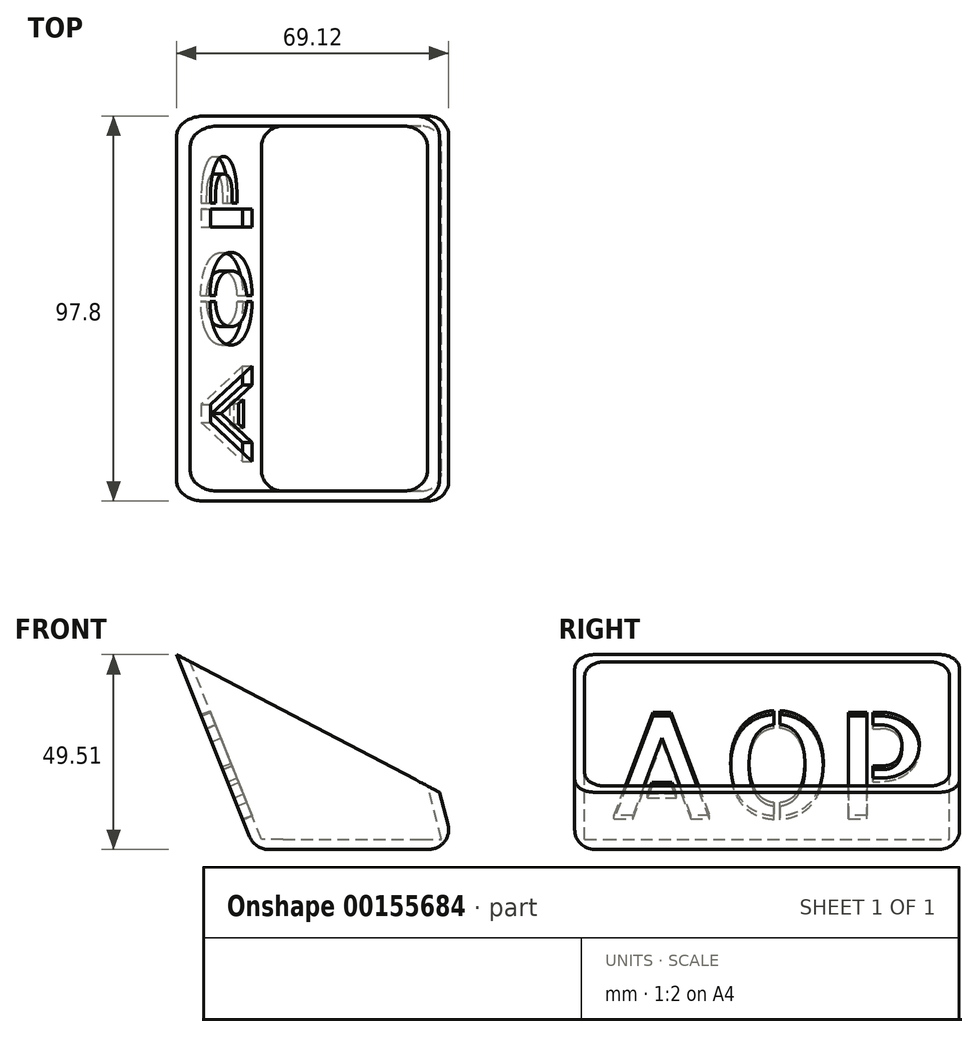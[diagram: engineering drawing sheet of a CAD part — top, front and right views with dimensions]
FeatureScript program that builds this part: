
annotation { "Feature Type Name" : "Feature", "Feature Type Description" : "" }
export const myFeature = defineFeature(function(context is Context, id is Id, definition is map)
    precondition{}
    {
        {
            var Q0;
            Q0=qCreatedBy(makeId("Front.planeOp"),FACE);
            var sketch = newSketch(context, id + "F0", { "sketchPlane" : qUnion([Q0])});
            skLineSegment(sketch, "E0", {"start": v(-16.22, 0) * mm, "end": v(34.58, 0) * mm});
            skLineSegment(sketch, "E1", {"start": v(34.58, 0) * mm, "end": v(30.69, 14.52) * mm});
            skLineSegment(sketch, "E2", {"start": v(-16.22, 0) * mm, "end": v(-36.08, 49.5) * mm});
            skLineSegment(sketch, "E3", {"start": v(-36.08, 49.5) * mm, "end": v(30.69, 14.52) * mm});
            skSolve(sketch);
        }
        {
            var Q0;
            Q0 = qSketchRegion(id + "F0", true);
            extrude(context, id + "F1", {"entities" : qUnion([Q0]), "endBound" : BoundingType.SYMMETRIC, "depth" : 97.8 * mm});
        }
        {
            var Q0;
            Q0=makeQuery(id+"F1.opExtrude","SWEPT_FACE",FACE,{"disambiguationData":[OSD([sQuery(id+"F0.wireOp",EDGE,"E3")])]});
            shell(context, id + "F2", {"entities" : qUnion([Q0]), "thickness" : 2.54 * mm});
        }
        {
            var Q0;
            Q0=makeQuery(id+"F1.opExtrude","CAP_EDGE",EDGE,{"disambiguationData":[OSD([sQuery(id+"F0.wireOp",EDGE,"E2")])],"isStart":false});
            var Q1;
            Q1=makeQuery(id+"F1.opExtrude","CAP_EDGE",EDGE,{"disambiguationData":[OSD([sQuery(id+"F0.wireOp",EDGE,"E1")])],"isStart":false});
            var Q2;
            Q2=makeQuery(id+"F1.opExtrude","CAP_EDGE",EDGE,{"disambiguationData":[OSD([sQuery(id+"F0.wireOp",EDGE,"E1")])],"isStart":true});
            var Q3;
            Q3=makeQuery(id+"F1.opExtrude","CAP_EDGE",EDGE,{"disambiguationData":[OSD([sQuery(id+"F0.wireOp",EDGE,"E2")])],"isStart":true});
            var Q4;
            Q4=makeQuery(id+"F1.opExtrude","SWEPT_EDGE",EDGE,{"disambiguationData":[OSD([sQuery(id+"F0.wireOp",EDGE,"E0"),sQuery(id+"F0.wireOp",EDGE,"E2")])]});
            var Q5;
            Q5=makeQuery(id+"F1.opExtrude","CAP_EDGE",EDGE,{"disambiguationData":[OSD([sQuery(id+"F0.wireOp",EDGE,"E0")])],"isStart":false});
            var Q6;
            Q6=makeQuery(id+"F1.opExtrude","CAP_EDGE",EDGE,{"disambiguationData":[OSD([sQuery(id+"F0.wireOp",EDGE,"E0")])],"isStart":true});
            var Q7;
            Q7=makeQuery(id+"F1.opExtrude","SWEPT_EDGE",EDGE,{"disambiguationData":[OSD([sQuery(id+"F0.wireOp",EDGE,"E0"),sQuery(id+"F0.wireOp",EDGE,"E1")])]});
            fillet(context, id + "F3", {"entities" : qUnion([Q0, Q1, Q2, Q3, Q4, Q5, Q6, Q7]), "radius" : 5.08 * mm, "tangentPropagation" : true, "allowEdgeOverflow" : false});
        }
        {
            var Q0;
            {var subQ0=sQuery(id+"F0.wireOp",EDGE,"E2");Q0=makeQuery(id+"F2.opShell","OFFSET_EDGE",EDGE,{"disambiguationData":[OSD([subQ0]),TDD([makeQuery(id+"F1.opExtrude","CAP_EDGE",EDGE,{"disambiguationData":[OSD([subQ0])],"isStart":false})])]});}
            var Q1;
            {var subQ0=sQuery(id+"F0.wireOp",EDGE,"E2");Q1=makeQuery(id+"F2.opShell","OFFSET_EDGE",EDGE,{"disambiguationData":[OSD([subQ0]),TDD([makeQuery(id+"F1.opExtrude","CAP_EDGE",EDGE,{"disambiguationData":[OSD([subQ0])],"isStart":true})])]});}
            var Q2;
            {var subQ0=sQuery(id+"F0.wireOp",EDGE,"E1");Q2=makeQuery(id+"F2.opShell","OFFSET_EDGE",EDGE,{"disambiguationData":[OSD([subQ0]),TDD([makeQuery(id+"F1.opExtrude","CAP_EDGE",EDGE,{"disambiguationData":[OSD([subQ0])],"isStart":true})])]});}
            var Q3;
            {var subQ0=sQuery(id+"F0.wireOp",EDGE,"E1");Q3=makeQuery(id+"F2.opShell","OFFSET_EDGE",EDGE,{"disambiguationData":[OSD([subQ0]),TDD([makeQuery(id+"F1.opExtrude","CAP_EDGE",EDGE,{"disambiguationData":[OSD([subQ0])],"isStart":false})])]});}
            fillet(context, id + "F4", {"entities" : qUnion([Q0, Q1, Q2, Q3]), "radius" : 5.08 * mm, "tangentPropagation" : true, "allowEdgeOverflow" : false});
        }
        {
            var Q0;
            Q0=makeQuery(id+"F2.opShell","OFFSET_FACE",FACE,{"disambiguationData":[OSD([sQuery(id+"F0.wireOp",EDGE,"E2")])]});
            var sketch = newSketch(context, id + "F5", { "sketchPlane" : qUnion([Q0])});
            skText(sketch, "E4", { "text": "AOP", "fontName": "AllertaStencil-Regular.ttf"});
            const initialGuessF5  = {"E4": [-0.04128, 0.01434, 1, 0, 0.02824]};
            skSetInitialGuess(sketch, initialGuessF5);
            skSolve(sketch);
        }
        {
            var Q0;
            Q0 = qSketchRegion(id + "F5", true);
            extrude(context, id + "F6", {"entities" : qUnion([Q0]), "operationType" : NewBodyOperationType.REMOVE, "oppositeDirection" : true, "depth" : 25.4 * mm});
        }
    });
